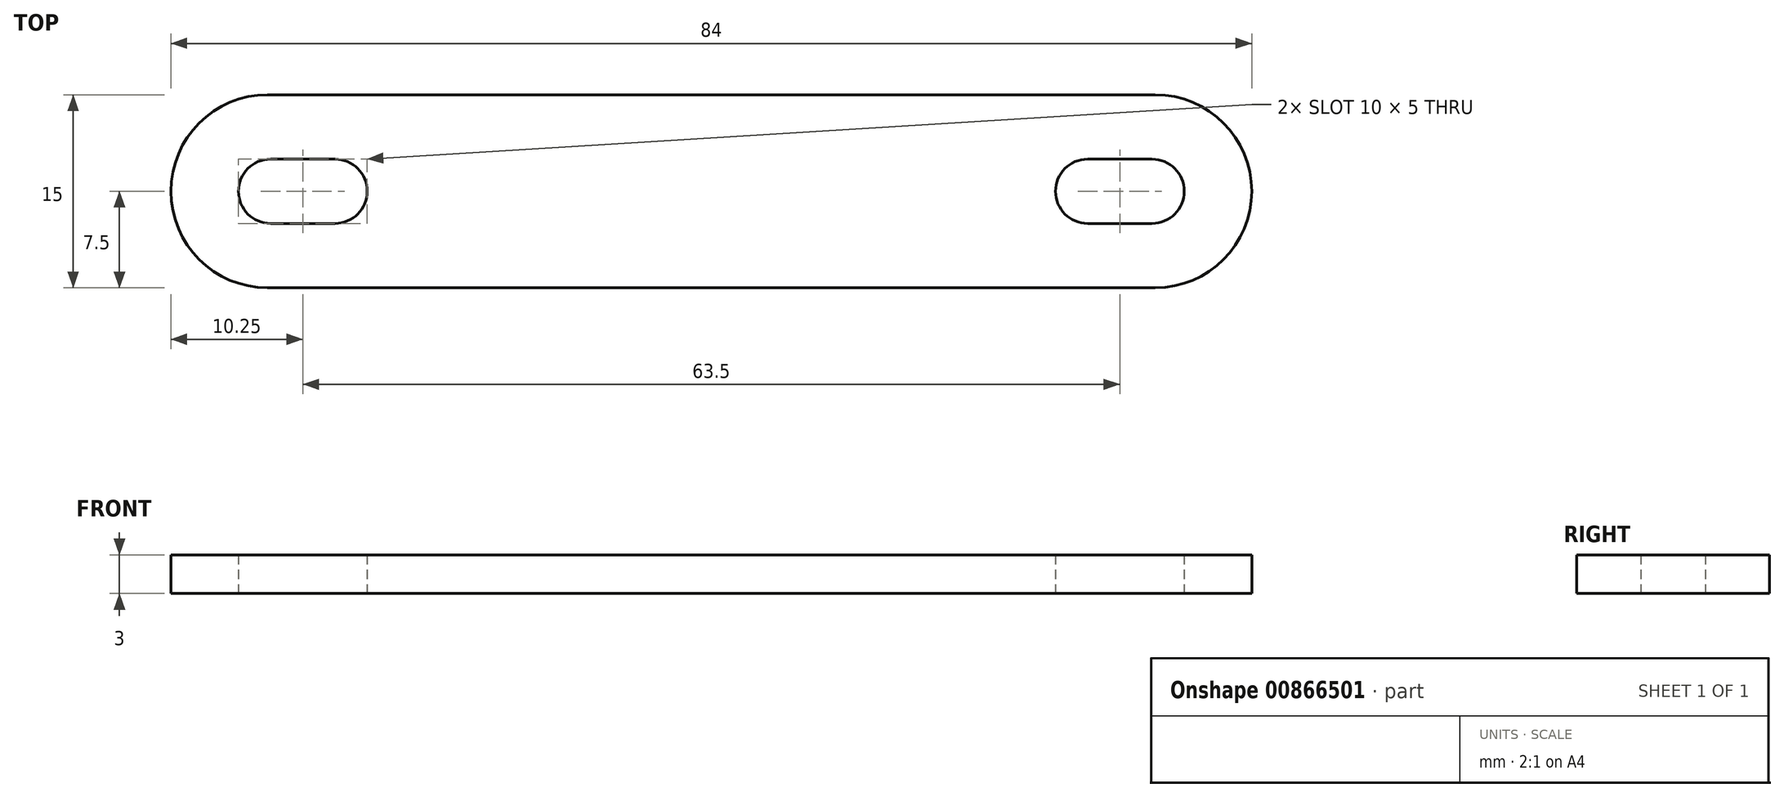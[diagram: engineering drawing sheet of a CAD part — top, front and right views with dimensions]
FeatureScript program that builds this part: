
annotation { "Feature Type Name" : "Feature", "Feature Type Description" : "" }
export const myFeature = defineFeature(function(context is Context, id is Id, definition is map)
    precondition{}
    {
        {
            var Q0;
            Q0=qCreatedBy(makeId("Top.planeOp"),FACE);
            var sketch = newSketch(context, id + "F0", { "sketchPlane" : qUnion([Q0])});
            skPoint(sketch, "E0", {"position": v(-31.75, 0) * mm});
            skLineSegment(sketch, "E1", {"start": v(-34.25, 0) * mm, "end": v(-29.25, 0) * mm});
            skArc(sketch, "E2.0.startCap", {"start": v(-34.25, -2.5) * mm, "mid": v(-36.75, 0) * mm, "end": v(-34.25, 2.5) * mm});
            skArc(sketch, "E2.0.endCap", {"start": v(-29.25, 2.5) * mm, "mid": v(-26.75, 0) * mm, "end": v(-29.25, -2.5) * mm});
            skLineSegment(sketch, "E2.0.left", {"start": v(-34.25, 2.5) * mm, "end": v(-29.25, 2.5) * mm});
            skLineSegment(sketch, "E2.0.right", {"start": v(-34.25, -2.5) * mm, "end": v(-29.25, -2.5) * mm});
            skLineSegment(sketch, "E3.bottom", {"start": v(0, 7.5) * mm, "end": v(-34.5, 7.5) * mm});
            skLineSegment(sketch, "E3.top", {"start": v(0, -7.5) * mm, "end": v(-34.5, -7.5) * mm});
            skLineSegment(sketch, "E3.left", {"start": v(0, 7.5) * mm, "end": v(0, -7.5) * mm});
            skLineSegment(sketch, "E3.right", {"start": v(-42, 0) * mm, "end": v(-42, 0) * mm});
            skPoint(sketch, "E4.visualSharp", {"position": v(-42, 7.5) * mm});
            skArc(sketch, "E4.filletArc", {"start": v(-34.5, 7.5) * mm, "mid": v(-39.8, 5.3) * mm, "end": v(-42, 0) * mm});
            skPoint(sketch, "E5.visualSharp", {"position": v(-42, -7.5) * mm});
            skArc(sketch, "E5.filletArc", {"start": v(-42, 0) * mm, "mid": v(-39.8, -5.3) * mm, "end": v(-34.5, -7.5) * mm});
            skLineSegment(sketch, "E6.MirrorCS", {"start": v(0, 7.5) * mm, "end": v(34.5, 7.5) * mm});
            skArc(sketch, "E7.MirrorCS", {"start": v(34.5, 7.5) * mm, "mid": v(39.8, 5.3) * mm, "end": v(42, 0) * mm});
            skLineSegment(sketch, "E8.MirrorCS", {"start": v(42, 0) * mm, "end": v(42, 0) * mm});
            skArc(sketch, "E9.MirrorCS", {"start": v(42, 0) * mm, "mid": v(39.8, -5.3) * mm, "end": v(34.5, -7.5) * mm});
            skLineSegment(sketch, "E10.MirrorCS", {"start": v(0, -7.5) * mm, "end": v(34.5, -7.5) * mm});
            skArc(sketch, "E11.MirrorCS", {"start": v(29.25, 2.5) * mm, "mid": v(26.75, 0) * mm, "end": v(29.25, -2.5) * mm});
            skArc(sketch, "E12.MirrorCS", {"start": v(34.25, -2.5) * mm, "mid": v(36.75, 0) * mm, "end": v(34.25, 2.5) * mm});
            skLineSegment(sketch, "E13.MirrorCS", {"start": v(34.25, -2.5) * mm, "end": v(29.25, -2.5) * mm});
            skLineSegment(sketch, "E14.MirrorCS", {"start": v(34.25, 2.5) * mm, "end": v(29.25, 2.5) * mm});
            skSolve(sketch);
        }
        {
            var Q0;
            Q0 = qSketchRegion(id + "F0", true);
            extrude(context, id + "F1", {"entities" : qUnion([Q0]), "depth" : 3 * mm, "offsetDistance" : 25 * mm});
        }
    });
